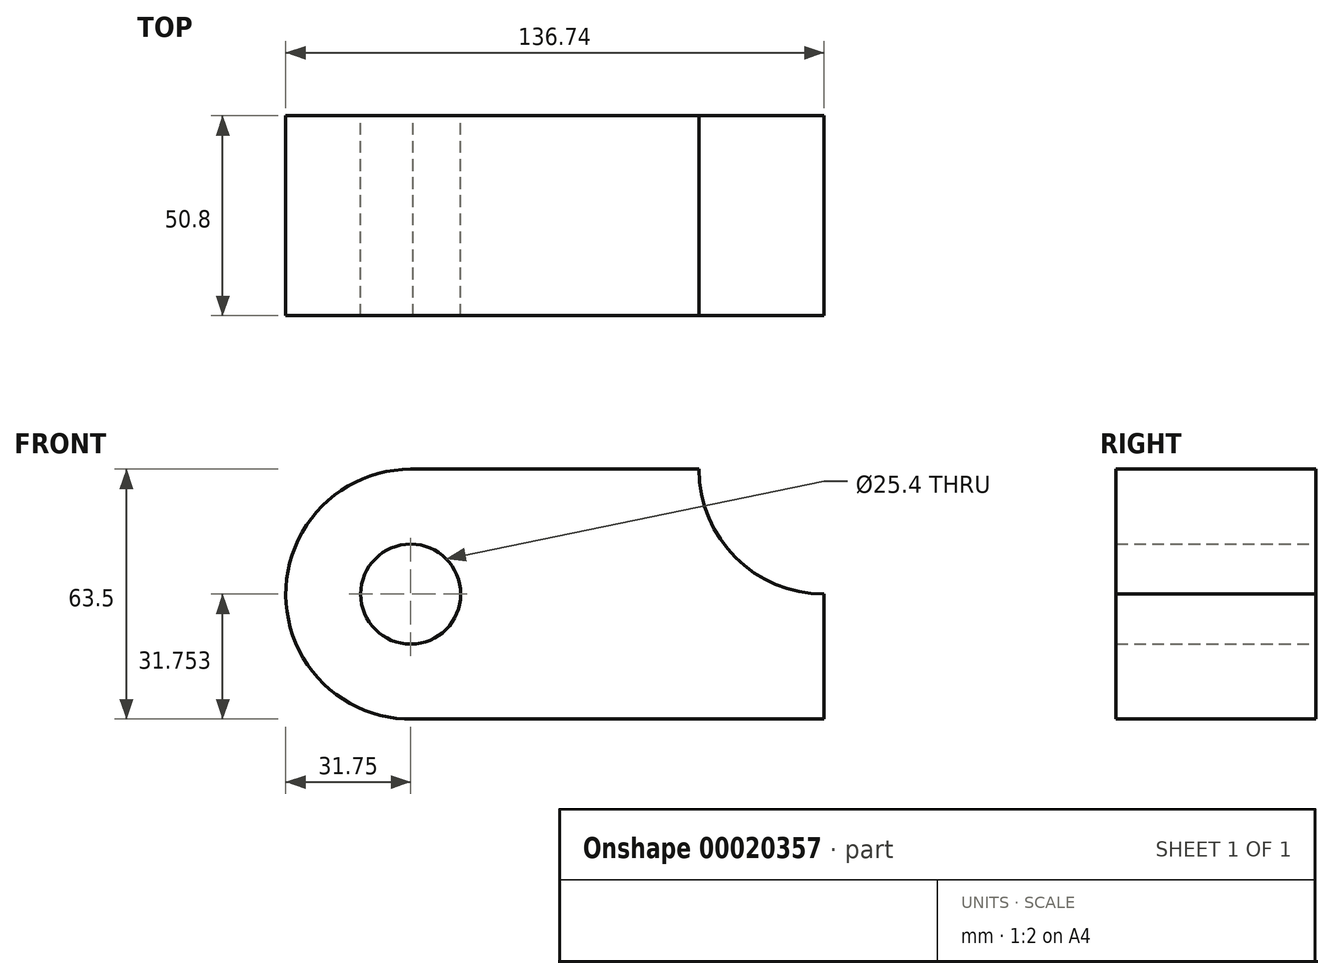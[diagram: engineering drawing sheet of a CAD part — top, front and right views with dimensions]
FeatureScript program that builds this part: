
annotation { "Feature Type Name" : "Feature", "Feature Type Description" : "" }
export const myFeature = defineFeature(function(context is Context, id is Id, definition is map)
    precondition{}
    {
        {
            var Q0;
            Q0=qCreatedBy(makeId("Front.planeOp"),FACE);
            var sketch = newSketch(context, id + "F0", { "sketchPlane" : qUnion([Q0])});
            skCircle(sketch, "E0", {"center": v(-53.39, 15.43) * mm, "radius": 12.7 * mm});
            skArc(sketch, "E1", {"start": v(19.85, 47.18) * mm, "mid": v(29.15, 24.73) * mm, "end": v(51.6, 15.43) * mm});
            skPoint(sketch, "E2.start.orphan", {"position": v(29.15, 24.73) * mm});
            skLineSegment(sketch, "E3", {"start": v(51.6, 15.43) * mm, "end": v(51.6, -16.32) * mm});
            skArc(sketch, "E4", {"start": v(-53.39, 47.18) * mm, "mid": v(-85.14, 15.15) * mm, "end": v(-52.83, -16.31) * mm});
            skLineSegment(sketch, "E5", {"start": v(-53.39, 47.18) * mm, "end": v(19.85, 47.18) * mm});
            skLineSegment(sketch, "E6", {"start": v(-52.83, -16.31) * mm, "end": v(51.6, -16.32) * mm});
            skSolve(sketch);
        }
        {
            var Q0;
            Q0=makeQuery(id+"F0.imprint","IMPRINT",FACE,{"disambiguationData":[TD([[makeQuery(id+"F0.imprint","IMPRINT",EDGE,{"derivedFrom":sQuery(id+"F0.wireOp",EDGE,"E0")}),-1.0]])]});
            extrude(context, id + "F1", {"entities" : qUnion([Q0]), "depth" : 50.8 * mm});
        }
    });
